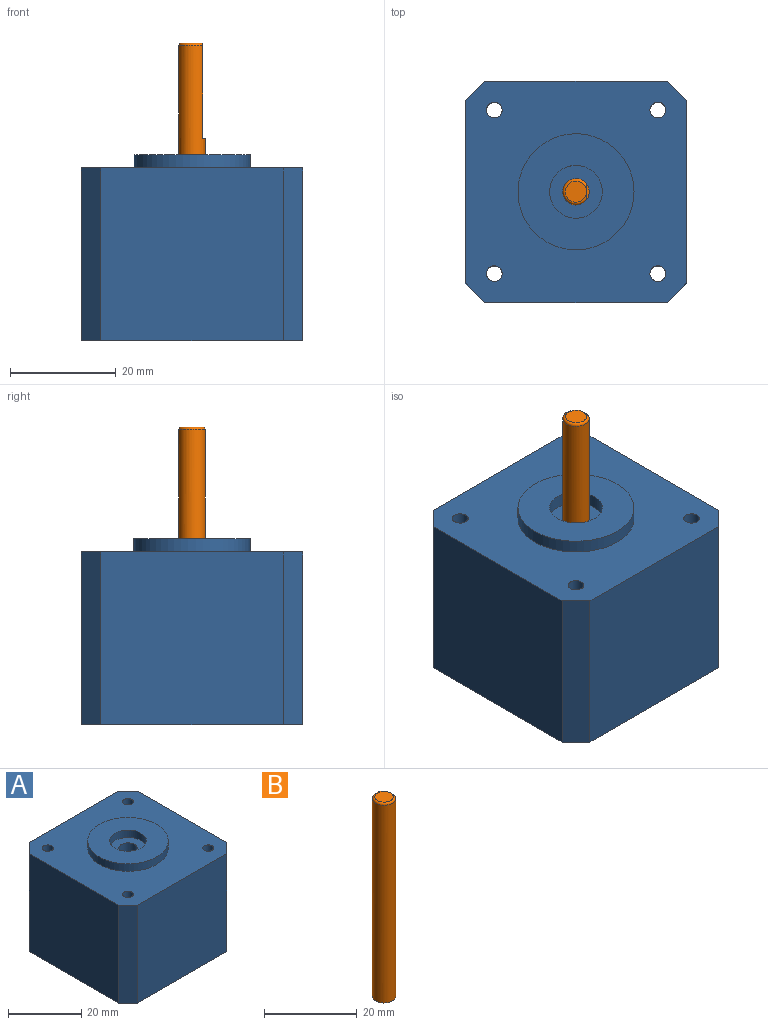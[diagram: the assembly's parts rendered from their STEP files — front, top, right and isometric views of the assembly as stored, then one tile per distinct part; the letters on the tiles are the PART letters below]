
ASSEMBLY  parts=2 mates=1
PART A: 21 faces, bbox 42x42x35.3 mm
  f0: cylinder r=2.5mm len=29mm, axis (0,0,1), area 455.5mm2, adj f1,f20
  f1: plane 10x10mm, normal (0,0,1), area 58.9mm2, adj f0,f16
  f2: plane 34.5x32.75mm, normal (-1,0,0), area 1129.9mm2, adj f3,f5,f14,f15
  f3: plane 42x42mm, normal (0,0,-1), area 1644mm2, adj f2,f4,f6,f7,f8,f9,f10,f11
  f4: plane 34.5x32.75mm, normal (1,0,0), area 1129.9mm2, adj f3,f5,f12,f13
  f5: plane 42x42mm, normal (0,0,1), area 1327.5mm2, adj f2,f4,f6,f7,f8,f9,f10,f11
  f6: plane 34.5x32.75mm, normal (0,-1,0), area 1129.9mm2, adj f3,f5,f13,f14
  f7: plane 34.5x32.75mm, normal (0,1,0), area 1129.9mm2, adj f3,f5,f12,f15
  f8: cylinder r=1.5mm len=32.75mm, axis (0,0,1), area 308.7mm2, adj f3,f5
  f9: cylinder r=1.5mm len=32.75mm, axis (0,0,1), area 308.7mm2, adj f3,f5
  f10: cylinder r=1.5mm len=32.75mm, axis (0,0,1), area 308.7mm2, adj f3,f5
  f11: cylinder r=1.5mm len=32.75mm, axis (0,0,1), area 308.7mm2, adj f3,f5
  f12: plane 32.75x3.75mm, normal (0.71,0.71,0), area 173.7mm2, adj f3,f4,f5,f7
  f13: plane 32.75x3.75mm, normal (0.71,-0.71,0), area 173.7mm2, adj f3,f4,f5,f6
  f14: plane 32.75x3.75mm, normal (-0.71,-0.71,0), area 173.7mm2, adj f2,f3,f5,f6
  f15: plane 32.75x3.75mm, normal (-0.71,0.71,0), area 173.7mm2, adj f2,f3,f5,f7
  f16: cylinder r=5mm len=10mm, axis (0,0,-1), area 78.5mm2, adj f1,f18
  f17: cylinder r=11mm len=22mm, axis (0,0,-1), area 172.8mm2, adj f5,f18
  f18: plane 22x22mm, normal (0,0,1), area 301.6mm2, adj f16,f17
  f19: cylinder r=4.5mm len=9mm, axis (0,0,-1), area 106mm2, adj f3,f20
  f20: plane 9x9mm, normal (0,0,-1), area 44mm2, adj f0,f19
PART B: 6 faces, bbox 5.4x5.4x52.8 mm
  f0: cylinder r=2.5mm len=52.25mm, axis (0,0,-1), area 764.4mm2, adj f2,f3,f4,f5
  f1: plane 4x4mm, normal (0,0,1), area 12.6mm2, adj f5
  f2: plane 5x5mm, normal (0,0,-1), area 19.6mm2, adj f0
  f3: plane 18x3mm, normal (1,0,0), area 53.8mm2, adj f0,f4,f5
  f4: plane 3x0.5mm, normal (0,0,1), area 1mm2, adj f0,f3
  f5: torus R=2mm, axis (0,0,1), area 9.6mm2, adj f0,f1,f3
PLACE A t=(-21,21,-9.6)mm
PLACE B t=(0,0,-5.95)mm
MATE revolute B.f0 <-> A.f0  axis (0,0,-1) through (0,0,-5.95)mm
